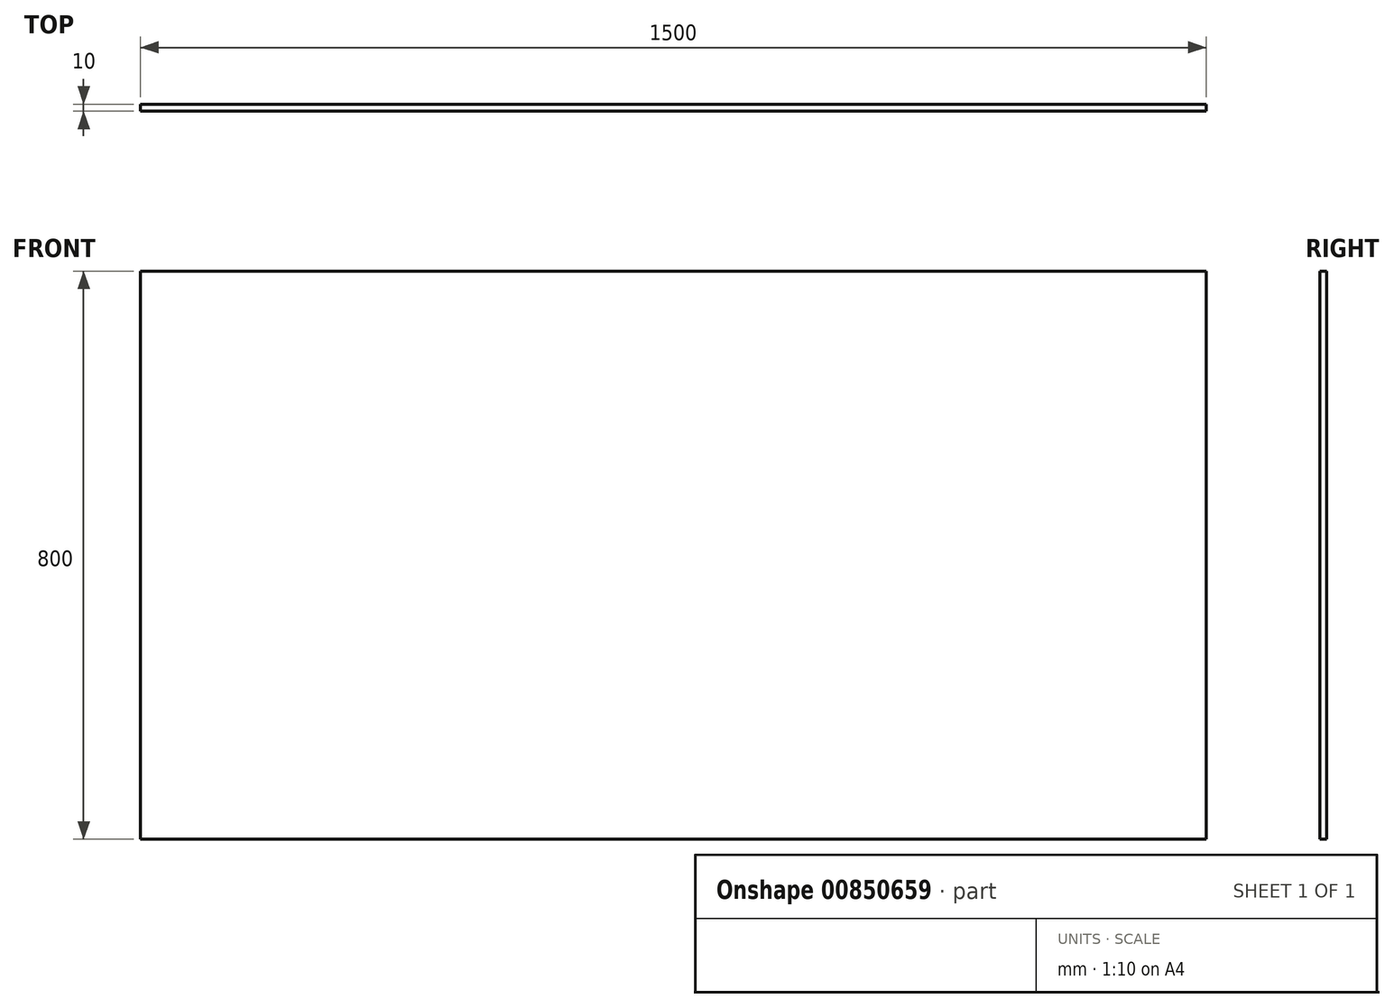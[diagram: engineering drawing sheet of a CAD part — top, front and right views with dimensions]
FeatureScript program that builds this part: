
annotation { "Feature Type Name" : "Feature", "Feature Type Description" : "" }
export const myFeature = defineFeature(function(context is Context, id is Id, definition is map)
    precondition{}
    {
        {
            var Q0;
            Q0=qCreatedBy(makeId("Front.planeOp"),FACE);
            var sketch = newSketch(context, id + "F0", { "sketchPlane" : qUnion([Q0])});
            skLineSegment(sketch, "E0.bottom", {"start": v(-1894.87, 756.3) * mm, "end": v(-394.87, 756.3) * mm});
            skLineSegment(sketch, "E0.top", {"start": v(-1894.87, -43.7) * mm, "end": v(-394.87, -43.7) * mm});
            skLineSegment(sketch, "E0.left", {"start": v(-1894.87, 756.3) * mm, "end": v(-1894.87, -43.7) * mm});
            skLineSegment(sketch, "E0.right", {"start": v(-394.87, 756.3) * mm, "end": v(-394.87, -43.7) * mm});
            skSolve(sketch);
        }
        {
            var Q0;
            Q0 = qSketchRegion(id + "F0", true);
            extrude(context, id + "F1", {"entities" : qUnion([Q0]), "depth" : 10 * mm, "offsetDistance" : 25 * mm});
        }
    });
